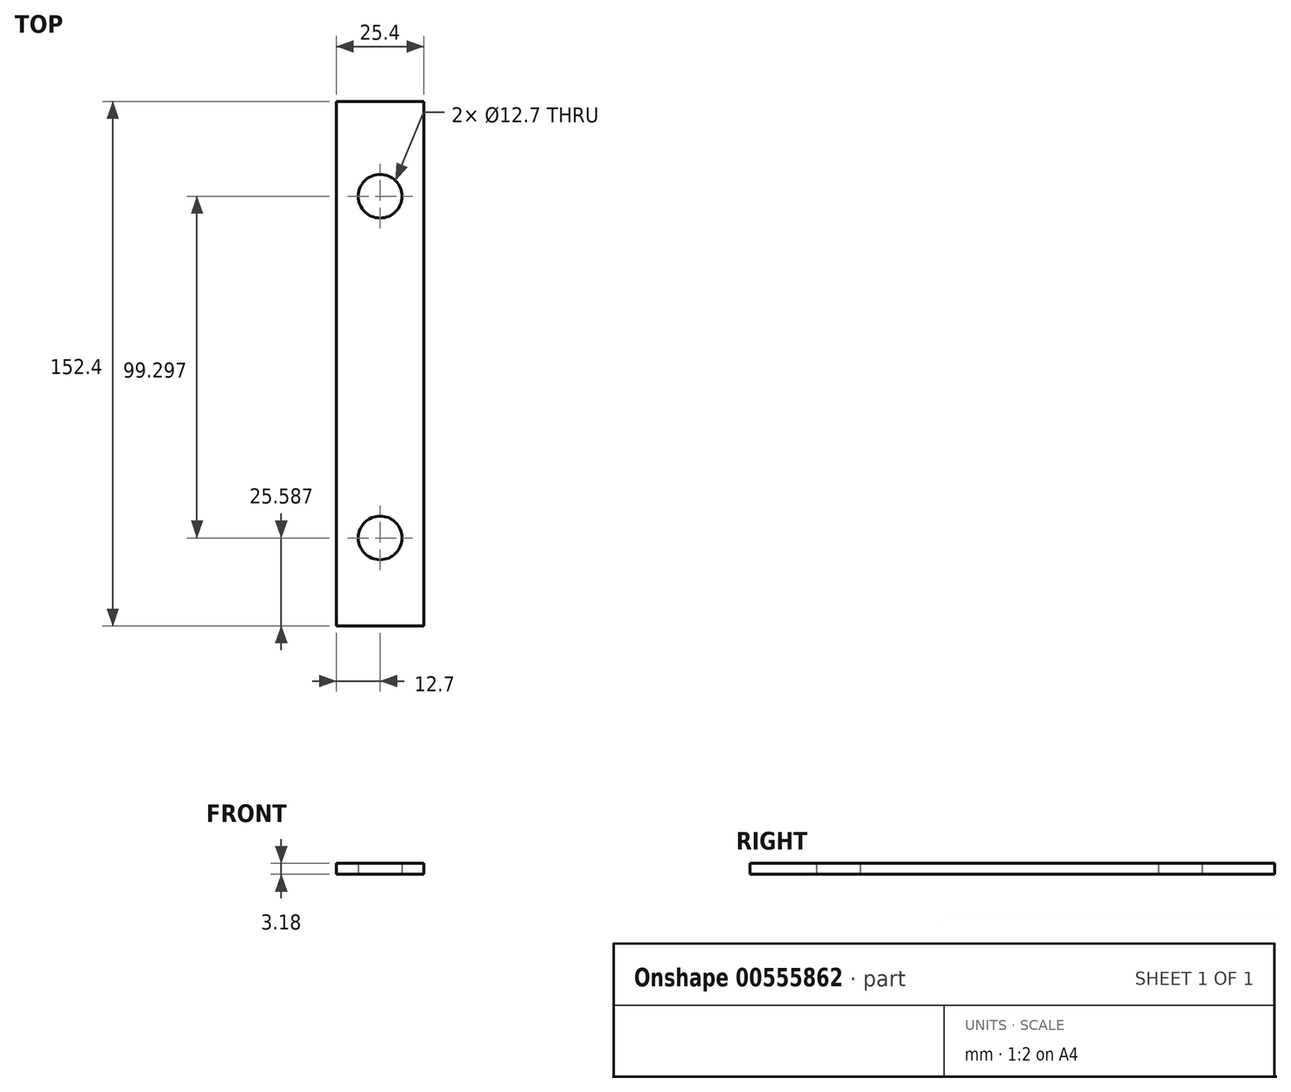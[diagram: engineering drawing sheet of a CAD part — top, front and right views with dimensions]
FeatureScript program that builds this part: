
annotation { "Feature Type Name" : "Feature", "Feature Type Description" : "" }
export const myFeature = defineFeature(function(context is Context, id is Id, definition is map)
    precondition{}
    {
        {
            var Q0;
            Q0=qCreatedBy(makeId("Top.planeOp"),FACE);
            var sketch = newSketch(context, id + "F0", { "sketchPlane" : qUnion([Q0])});
            skLineSegment(sketch, "E0.bottom", {"start": v(-12.7, -76.2) * mm, "end": v(12.7, -76.2) * mm});
            skLineSegment(sketch, "E0.top", {"start": v(-12.7, 76.2) * mm, "end": v(12.7, 76.2) * mm});
            skLineSegment(sketch, "E0.left", {"start": v(-12.7, -76.2) * mm, "end": v(-12.7, 76.2) * mm});
            skLineSegment(sketch, "E0.right", {"start": v(12.7, -76.2) * mm, "end": v(12.7, 76.2) * mm});
            skPoint(sketch, "E0.middle", {"position": v(0, 0) * mm});
            skSolve(sketch);
        }
        {
            var Q0;
            Q0=makeQuery(id+"F0.imprint","IMPRINT",FACE,{"disambiguationData":[TD([[makeQuery(id+"F0.imprint","IMPRINT",EDGE,{"derivedFrom":sQuery(id+"F0.wireOp",EDGE,"E0.bottom")}),1.0]])]});
            extrude(context, id + "F1", {"entities" : qUnion([Q0]), "depth" : 3.17 * mm, "offsetDistance" : 25.4 * mm});
        }
        {
            var Q0;
            Q0=qCreatedBy(makeId("Top.planeOp"),FACE);
            var sketch = newSketch(context, id + "F2", { "sketchPlane" : qUnion([Q0])});
            skCircle(sketch, "E1", {"center": v(0, 48.68) * mm, "radius": 6.35 * mm});
            skCircle(sketch, "E2", {"center": v(0, -50.61) * mm, "radius": 6.35 * mm});
            skSolve(sketch);
        }
        {
            var Q0;
            Q0=sQuery(id+"F2.wireOp",VERTEX,"E1.center");
            var Q1;
            Q1=makeQuery(id+"F1.opExtrude","SWEPT_BODY",BODY,{"disambiguationData":[OSD([sQuery(id+"F0.wireOp",EDGE,"E0.bottom"),sQuery(id+"F0.wireOp",EDGE,"E0.top"),sQuery(id+"F0.wireOp",EDGE,"E0.left"),sQuery(id+"F0.wireOp",EDGE,"E0.right")])]});
            hole(context, id + "F3", {"style" : HoleStyle.SIMPLE, "endStyle" : HoleEndStyle.BLIND, "oppositeDirection" : true, "holeDiameter" : 12.7 * mm, "holeDepth" : 25.4 * mm, "isTappedThrough" : true, "tappedDepth" : 12.7 * mm, "tapClearance" : 3, "startFromSketch" : true, "locations" : qUnion([Q0]), "scope" : qUnion([Q1])});
        }
        {
            var Q0;
            Q0=sQuery(id+"F2.wireOp",VERTEX,"E2.center");
            var Q1;
            Q1=makeQuery(id+"F1.opExtrude","SWEPT_BODY",BODY,{"disambiguationData":[OSD([sQuery(id+"F0.wireOp",EDGE,"E0.bottom"),sQuery(id+"F0.wireOp",EDGE,"E0.top"),sQuery(id+"F0.wireOp",EDGE,"E0.left"),sQuery(id+"F0.wireOp",EDGE,"E0.right")])]});
            hole(context, id + "F4", {"style" : HoleStyle.SIMPLE, "endStyle" : HoleEndStyle.BLIND, "oppositeDirection" : true, "holeDiameter" : 12.7 * mm, "holeDepth" : 25.4 * mm, "isTappedThrough" : true, "tappedDepth" : 12.7 * mm, "tapClearance" : 3, "startFromSketch" : true, "locations" : qUnion([Q0]), "scope" : qUnion([Q1])});
        }
    });
